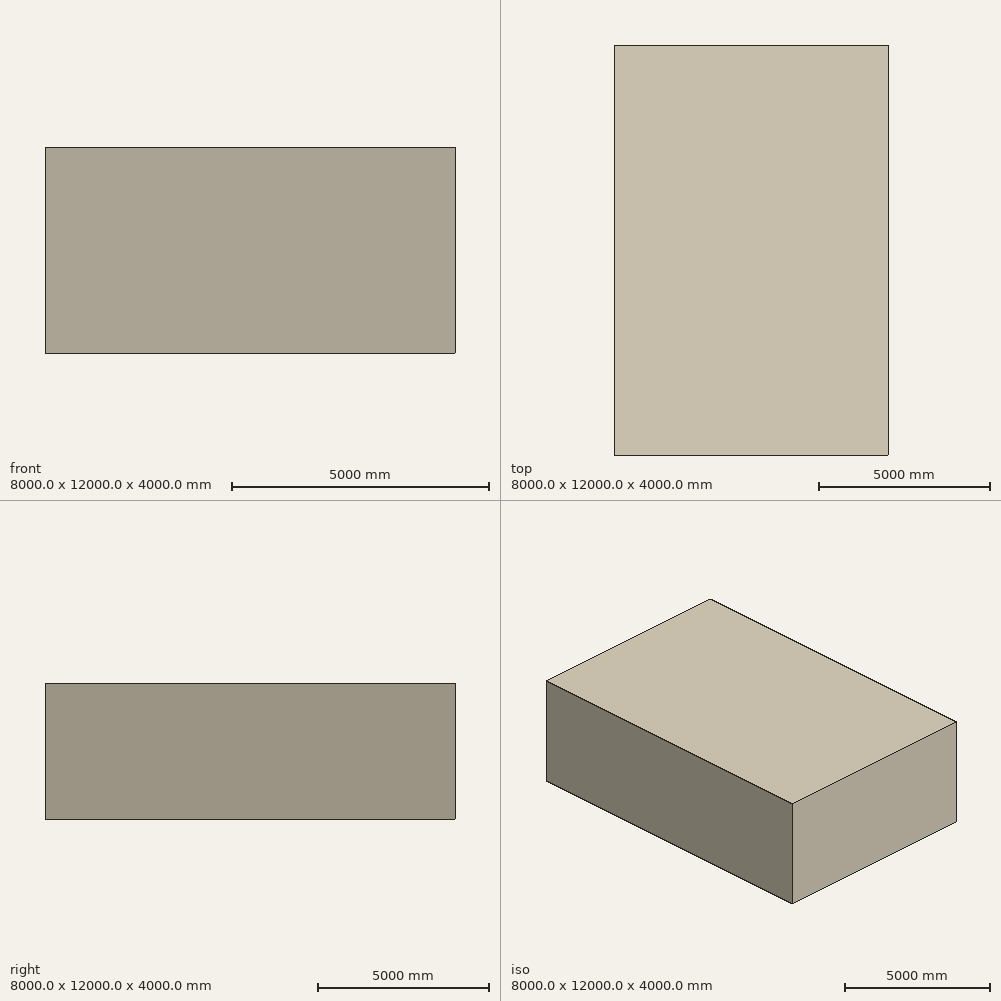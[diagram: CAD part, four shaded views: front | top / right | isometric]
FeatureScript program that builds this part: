
annotation { "Feature Type Name" : "Feature", "Feature Type Description" : "" }
export const myFeature = defineFeature(function(context is Context, id is Id, definition is map)
    precondition{}
    {
        {
            var Q0;
            Q0=qCreatedBy(makeId("Front.planeOp"),FACE);
            var sketch = newSketch(context, id + "F0", { "sketchPlane" : qUnion([Q0])});
            skLineSegment(sketch, "E0", {"start": v(-4000, -1116.87) * mm, "end": v(4000, -1116.87) * mm});
            skLineSegment(sketch, "E1", {"start": v(4000, -1116.87) * mm, "end": v(4000, 2883.13) * mm});
            skLineSegment(sketch, "E2", {"start": v(4000, 2883.13) * mm, "end": v(0, 2883.13) * mm});
            skLineSegment(sketch, "E3", {"start": v(-4000, -1116.87) * mm, "end": v(-4000, 2883.13) * mm});
            skLineSegment(sketch, "E4", {"start": v(-4000, 2883.13) * mm, "end": v(0, 2883.13) * mm});
            skSolve(sketch);
        }
        {
            var Q0;
            Q0 = qSketchRegion(id + "F0", true);
            extrude(context, id + "F1", {"entities" : qUnion([Q0]), "depth" : 12000 * mm});
        }
    });
